# Revit family: ML21 - 6 Degree Angle
name_source: partatom
category: Generic Models
revit_build: Autodesk Revit Architecture 2012 (Build: 20110309_2315(x64)
units: mm (PartAtom-declared; Revit-internal decimal feet)

## types (3) — shared parameters
Back Shelf Depth = 1' - 10"
Front Shelf Depth = 1' - 10"
Model = Maxi Line System - Spacer System for Curved Gondola
URL = http://www.madixinc.com

## per-type parameters (varying)
| type | 3' Back Base Spacer | 3' Back Spacer 2' | 3' Back Spacer 3'-6" | 3' Back Spacer 5' | 3' Back Spacer 6'-6" | 3' Front Base Spacer | 3' Front Spacer 2' | 3' Front Spacer 3'-6" | 3' Front Spacer 5' | 3' Front Spacer 6'-6" | 4' Back Base Spacer | 4' Back Spacer 2' | 4' Back Spacer 3'-6" | 4' Back Spacer 5' | 4' Back Spacer 6'-6" | 4' Front Base Spacer | 4' Front Spacer 2' | 4' Front Spacer 3'-6" | 4' Front Spacer 5' | 4' Front Spacer 6'-6" | Width |
| ML21 | No | No | No | No | No | No | No | No | No | No | No | No | No | No | No | No | No | No | No | No | 3' - 0" |
| ML21 - 3' | Yes | Yes | Yes | Yes | Yes | Yes | Yes | Yes | Yes | Yes | No | No | No | No | No | No | No | No | No | No | 3' - 0" |
| ML21 - 4' | No | No | No | No | No | No | No | No | No | No | Yes | Yes | Yes | Yes | Yes | Yes | Yes | Yes | Yes | Yes | 4' - 0" |

## geometry (parser evidence)
native form markers: Blend x6, Sweep x3
no freeform markers — native parametric forms only
